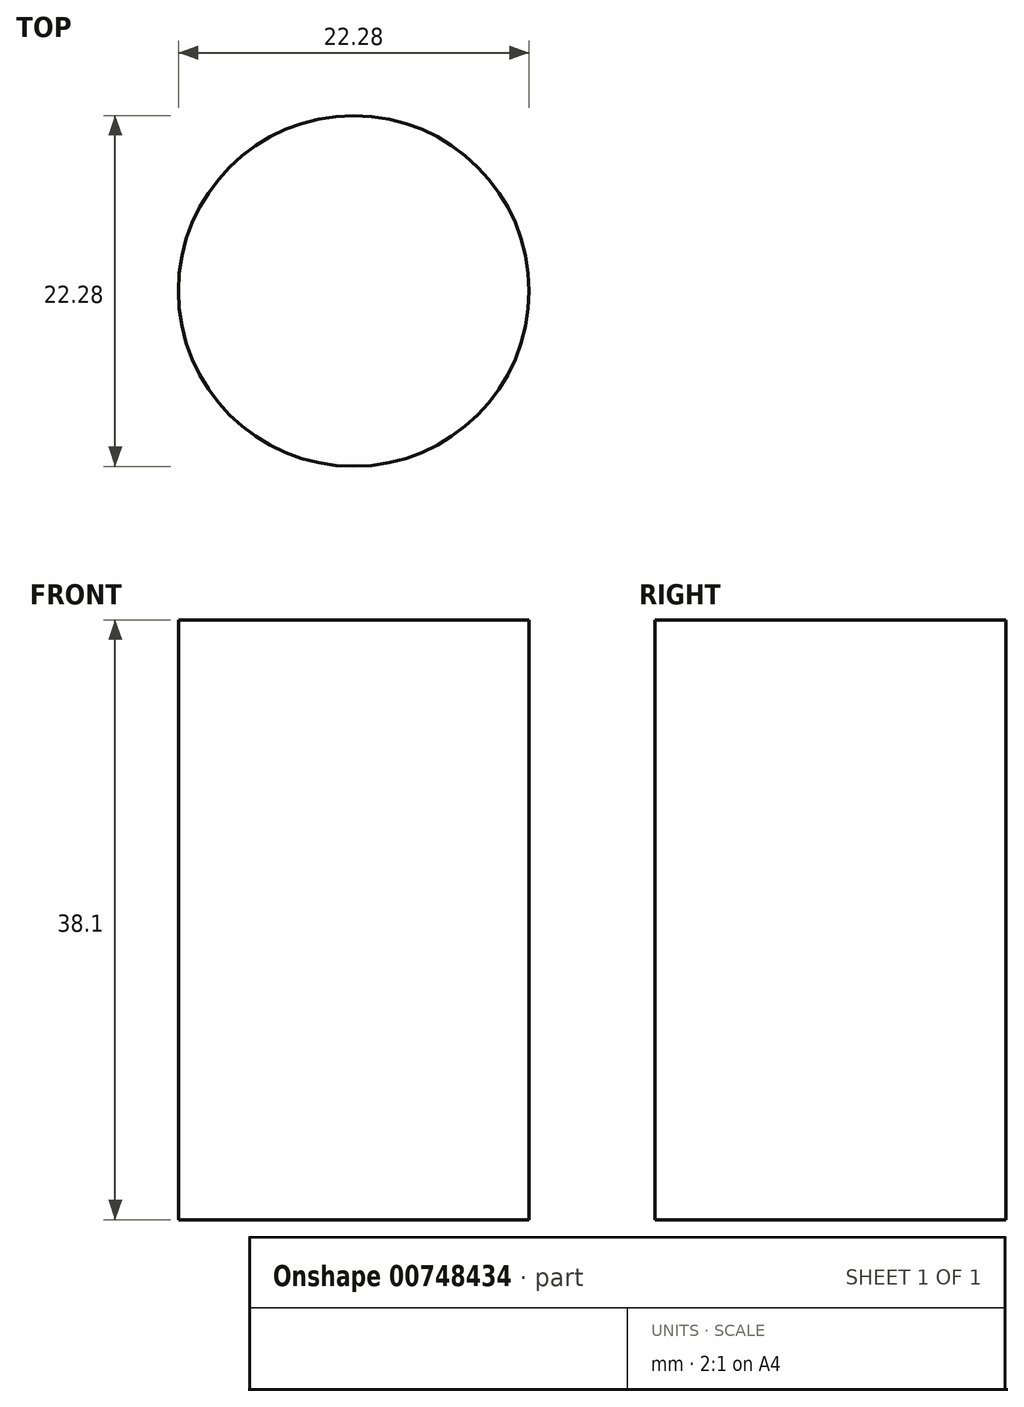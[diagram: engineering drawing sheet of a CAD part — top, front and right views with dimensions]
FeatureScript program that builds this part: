
annotation { "Feature Type Name" : "Feature", "Feature Type Description" : "" }
export const myFeature = defineFeature(function(context is Context, id is Id, definition is map)
    precondition{}
    {
        {
            var Q0;
            Q0=qCreatedBy(makeId("Top.planeOp"),FACE);
            var sketch = newSketch(context, id + "F0", { "sketchPlane" : qUnion([Q0])});
            skCircle(sketch, "E0", {"center": v(0, 0) * mm, "radius": 11.14 * mm});
            skSolve(sketch);
        }
        {
            var Q0;
            Q0 = qSketchRegion(id + "F0", true);
            extrude(context, id + "F1", {"entities" : qUnion([Q0]), "depth" : 38.1 * mm, "offsetDistance" : 25.4 * mm});
        }
    });
